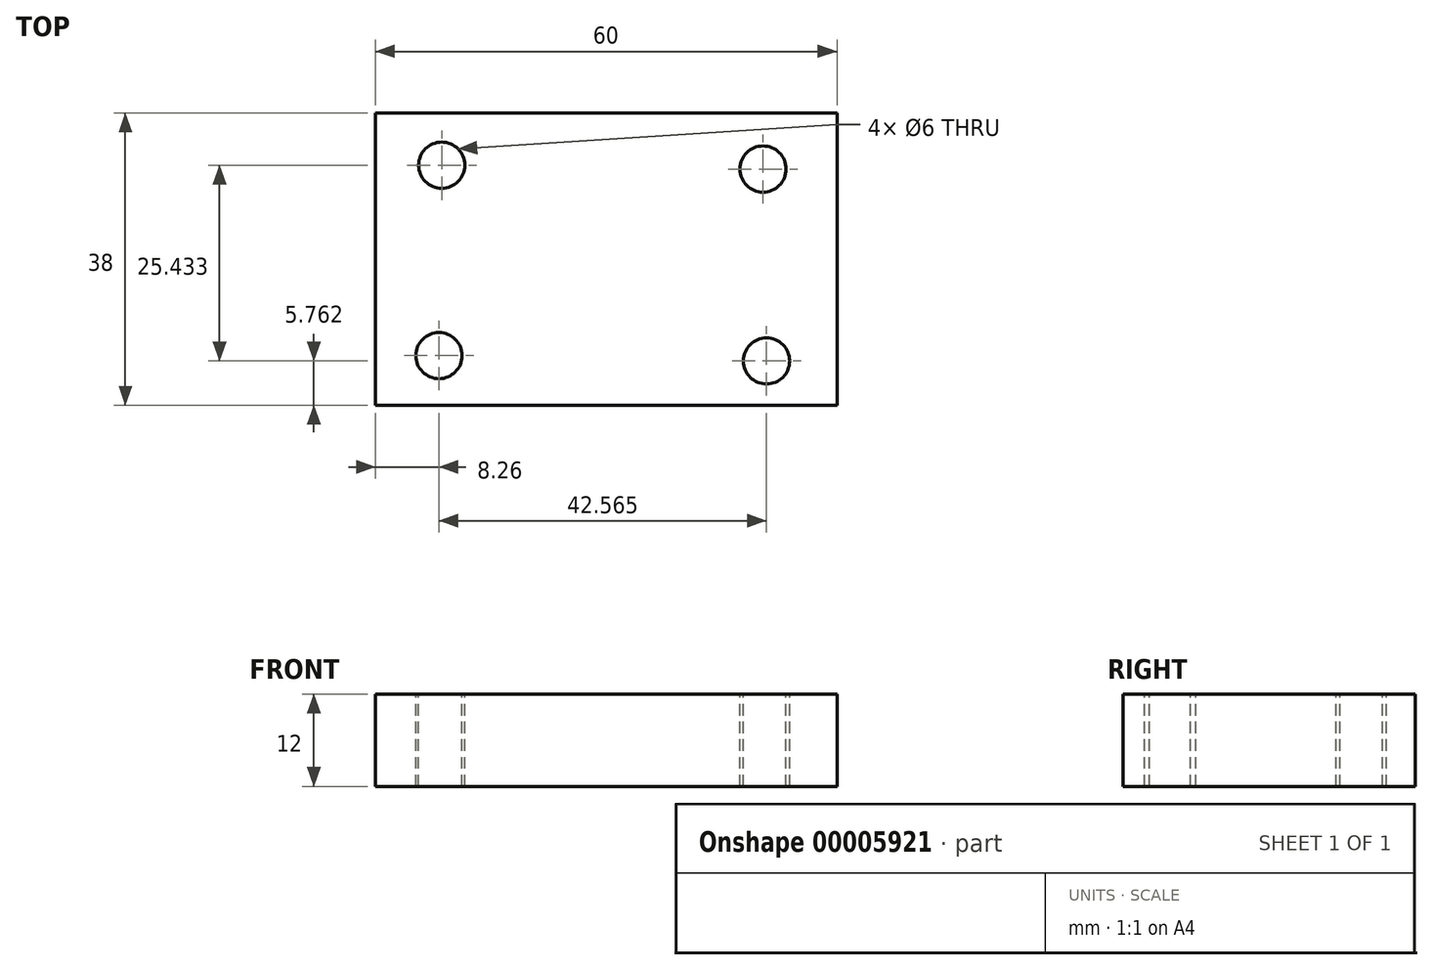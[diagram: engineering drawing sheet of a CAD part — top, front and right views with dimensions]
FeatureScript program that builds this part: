
annotation { "Feature Type Name" : "Feature", "Feature Type Description" : "" }
export const myFeature = defineFeature(function(context is Context, id is Id, definition is map)
    precondition{}
    {
        {
            var Q0;
            Q0=qCreatedBy(makeId("Top.planeOp"),FACE);
            var sketch = newSketch(context, id + "F0", { "sketchPlane" : qUnion([Q0])});
            skLineSegment(sketch, "E0.bottom", {"start": v(33.72, 23.04) * mm, "end": v(-26.28, 23.04) * mm});
            skLineSegment(sketch, "E0.top", {"start": v(33.72, -14.96) * mm, "end": v(-26.28, -14.96) * mm});
            skLineSegment(sketch, "E0.left", {"start": v(33.72, 23.04) * mm, "end": v(33.72, -14.96) * mm});
            skLineSegment(sketch, "E0.right", {"start": v(-26.28, 23.04) * mm, "end": v(-26.28, -14.96) * mm});
            skSolve(sketch);
        }
        {
            var Q0;
            Q0=makeQuery(id+"F0.imprint","IMPRINT",FACE,{"disambiguationData":[TD([[makeQuery(id+"F0.imprint","IMPRINT",EDGE,{"derivedFrom":sQuery(id+"F0.wireOp",EDGE,"E0.bottom")}),1.0]])]});
            extrude(context, id + "F1", {"entities" : qUnion([Q0]), "depth" : 12 * mm});
        }
        {
            var Q0;
            Q0=makeQuery(id+"F1.opExtrude","CAP_FACE",FACE,{"disambiguationData":[OSD([sQuery(id+"F0.wireOp",EDGE,"E0.bottom"),sQuery(id+"F0.wireOp",EDGE,"E0.top"),sQuery(id+"F0.wireOp",EDGE,"E0.left"),sQuery(id+"F0.wireOp",EDGE,"E0.right")])],"isStart":false});
            var sketch = newSketch(context, id + "F2", { "sketchPlane" : qUnion([Q0])});
            skCircle(sketch, "E1", {"center": v(-17.67, 16.23) * mm, "radius": 3 * mm});
            skSolve(sketch);
        }
        {
            var Q0;
            Q0=makeQuery(id+"F2.imprint","IMPRINT",FACE,{"disambiguationData":[TD([[makeQuery(id+"F2.imprint","IMPRINT",EDGE,{"derivedFrom":sQuery(id+"F2.wireOp",EDGE,"E1")}),-1.0]])]});
            var sketch = newSketch(context, id + "F3", { "sketchPlane" : qUnion([Q0])});
            skCircle(sketch, "E2", {"center": v(24.08, 15.74) * mm, "radius": 3 * mm});
            skSolve(sketch);
        }
        {
            var Q0;
            Q0=makeQuery(id+"F2.imprint","IMPRINT",FACE,{"disambiguationData":[TD([[makeQuery(id+"F2.imprint","IMPRINT",EDGE,{"derivedFrom":sQuery(id+"F2.wireOp",EDGE,"E1")}),-1.0]])]});
            var sketch = newSketch(context, id + "F4", { "sketchPlane" : qUnion([Q0])});
            skCircle(sketch, "E3", {"center": v(24.54, -9.2) * mm, "radius": 3 * mm});
            skSolve(sketch);
        }
        {
            var Q0;
            Q0=makeQuery(id+"F2.imprint","IMPRINT",FACE,{"disambiguationData":[TD([[makeQuery(id+"F2.imprint","IMPRINT",EDGE,{"derivedFrom":sQuery(id+"F2.wireOp",EDGE,"E1")}),-1.0]])]});
            var sketch = newSketch(context, id + "F5", { "sketchPlane" : qUnion([Q0])});
            skCircle(sketch, "E4", {"center": v(-18.02, -8.5) * mm, "radius": 3 * mm});
            skSolve(sketch);
        }
        {
            var Q0;
            Q0 = qSketchRegion(id + "F4", true);
            extrude(context, id + "F6", {"entities" : qUnion([Q0]), "operationType" : NewBodyOperationType.REMOVE, "oppositeDirection" : true, "depth" : 25 * mm});
        }
        {
            var Q0;
            Q0 = qSketchRegion(id + "F3", true);
            extrude(context, id + "F7", {"entities" : qUnion([Q0]), "operationType" : NewBodyOperationType.REMOVE, "oppositeDirection" : true, "depth" : 25 * mm});
        }
        {
            var Q0;
            Q0 = qSketchRegion(id + "F2", true);
            extrude(context, id + "F8", {"entities" : qUnion([Q0]), "operationType" : NewBodyOperationType.REMOVE, "oppositeDirection" : true, "depth" : 25 * mm});
        }
        {
            var Q0;
            Q0 = qSketchRegion(id + "F5", true);
            extrude(context, id + "F9", {"entities" : qUnion([Q0]), "operationType" : NewBodyOperationType.REMOVE, "oppositeDirection" : true, "depth" : 25 * mm});
        }
    });
